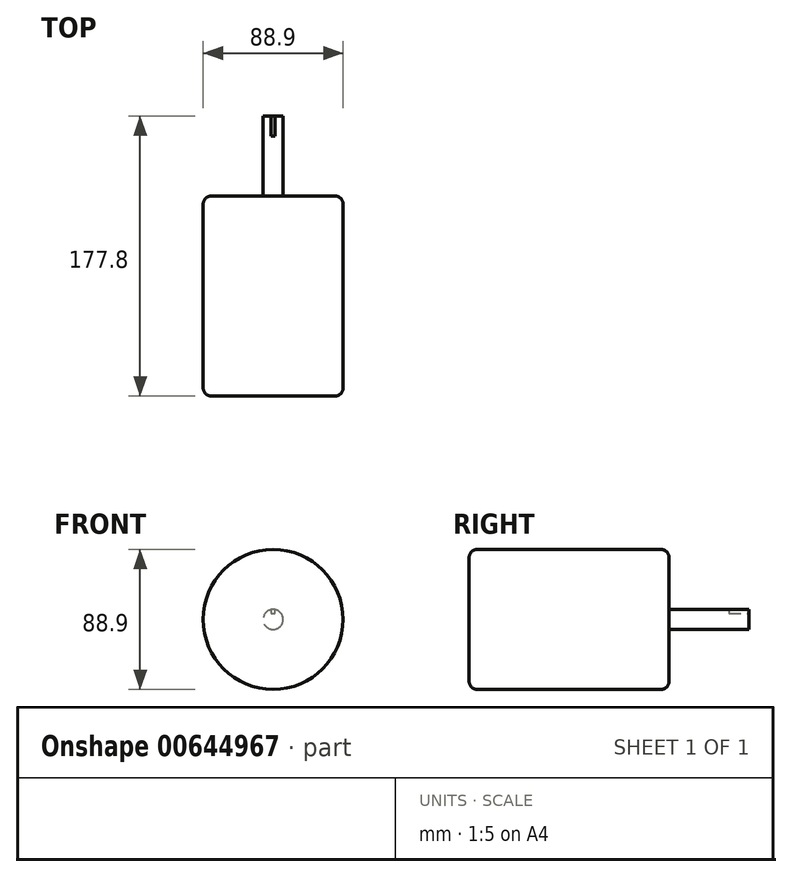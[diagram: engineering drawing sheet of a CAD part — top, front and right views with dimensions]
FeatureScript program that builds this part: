
annotation { "Feature Type Name" : "Feature", "Feature Type Description" : "" }
export const myFeature = defineFeature(function(context is Context, id is Id, definition is map)
    precondition{}
    {
        {
            var Q0;
            Q0=qCreatedBy(makeId("Front.planeOp"),FACE);
            var sketch = newSketch(context, id + "F0", { "sketchPlane" : qUnion([Q0])});
            skCircle(sketch, "E0", {"center": v(0, 0) * mm, "radius": 6.35 * mm});
            skSolve(sketch);
        }
        {
            var Q0;
            Q0 = qSketchRegion(id + "F0", true);
            extrude(context, id + "F1", {"entities" : qUnion([Q0]), "depth" : 50.8 * mm, "offsetDistance" : 25.4 * mm});
        }
        {
            var Q0;
            Q0=makeQuery(id+"F1.opExtrude","CAP_FACE",FACE,{"disambiguationData":[OSD([sQuery(id+"F0.wireOp",EDGE,"E0")])],"isStart":false});
            var sketch = newSketch(context, id + "F2", { "sketchPlane" : qUnion([Q0])});
            skCircle(sketch, "E1", {"center": v(0, 0) * mm, "radius": 44.45 * mm});
            skSolve(sketch);
        }
        {
            var Q0;
            Q0 = qSketchRegion(id + "F2", true);
            extrude(context, id + "F3", {"entities" : qUnion([Q0]), "operationType" : NewBodyOperationType.ADD, "depth" : 127 * mm, "offsetDistance" : 25.4 * mm});
        }
        {
            var Q0;
            Q0=makeQuery(id+"F3.opExtrude","CAP_EDGE",EDGE,{"disambiguationData":[OSD([sQuery(id+"F2.wireOp",EDGE,"E1")])],"isStart":true});
            fillet(context, id + "F4", {"entities" : qUnion([Q0]), "radius" : 5.08 * mm, "tangentPropagation" : true, "allowEdgeOverflow" : false});
        }
        {
            var Q0;
            Q0=makeQuery(id+"F3.opExtrude","CAP_EDGE",EDGE,{"disambiguationData":[OSD([sQuery(id+"F2.wireOp",EDGE,"E1")])],"isStart":false});
            fillet(context, id + "F5", {"entities" : qUnion([Q0]), "radius" : 5.08 * mm, "tangentPropagation" : true, "allowEdgeOverflow" : false});
        }
        {
            var Q0;
            Q0=makeQuery(id+"F1.opExtrude","CAP_FACE",FACE,{"disambiguationData":[OSD([sQuery(id+"F0.wireOp",EDGE,"E0")])],"isStart":true});
            var sketch = newSketch(context, id + "F6", { "sketchPlane" : qUnion([Q0])});
            skCircle(sketch, "E2", {"center": v(0, 0) * mm, "radius": 6.35 * mm});
            skLineSegment(sketch, "E3", {"start": v(0, 0) * mm, "end": v(0, 6.35) * mm});
            skLineSegment(sketch, "E4", {"start": v(1.27, 6.22) * mm, "end": v(1.27, 3.81) * mm});
            skLineSegment(sketch, "E5", {"start": v(1.27, 3.81) * mm, "end": v(-1.27, 3.81) * mm});
            skLineSegment(sketch, "E6", {"start": v(-1.27, 3.81) * mm, "end": v(-1.27, 6.22) * mm});
            skSolve(sketch);
        }
        {
            var Q0;
            {var subQ3=sQuery(id+"F6.wireOp",EDGE,"E6");Q0=makeQuery(id+"F6.imprint","IMPRINT",FACE,{"disambiguationData":[TD([[makeQuery(id+"F6.imprint","IMPRINT",EDGE,{"derivedFrom":subQ3}),-1.0]])]});}
            var Q1;
            {var subQ3=sQuery(id+"F6.wireOp",EDGE,"E4");Q1=makeQuery(id+"F6.imprint","IMPRINT",FACE,{"disambiguationData":[TD([[makeQuery(id+"F6.imprint","IMPRINT",EDGE,{"derivedFrom":subQ3}),-1.0]])]});}
            extrude(context, id + "F7", {"entities" : qUnion([Q0, Q1]), "operationType" : NewBodyOperationType.REMOVE, "oppositeDirection" : true, "depth" : 12.7 * mm, "offsetDistance" : 25.4 * mm});
        }
    });
